# Revit family: Furniture_Other-Furniture_Lammhults_Tension-Trolley
name_source: partatom
category: Furniture
units: mm (PartAtom-declared; Revit-internal decimal feet)

## family parameters
Always vertical = Yes
Cut with Voids When Loaded = No
OmniClass Number = 23.21.11.00
Room Calculation Point = No
Shared = No
Work Plane-Based = Yes

## types (2) — shared parameters
Default Elevation = 1219 mm
Depth = 453 mm
Frame Material = Lammhults - Powder Coated Steel - RAL 2004
Height = 614 mm
Manufacturer = Lammhults
Model = Tension Trolley
Product data url = https://www.bimobject.com
URL = https://www.lammhults.se
Version = 1
Width = 950 mm

## per-type parameters (varying)
| type | Shelves Material | with leather trim on shelves |
| W950 x D453 x H614 with leather trim on shelves | Lammhults - Powder Coated Steel - RAL 2004 | Yes |
| W950 x D453 x H614 without leather trim on shelves | Lammhults - Stainless | No |

note: column(s) folded — value = type name in every type: Description

## geometry (parser evidence)
native form markers: Sweep x2
no freeform markers — native parametric forms only
